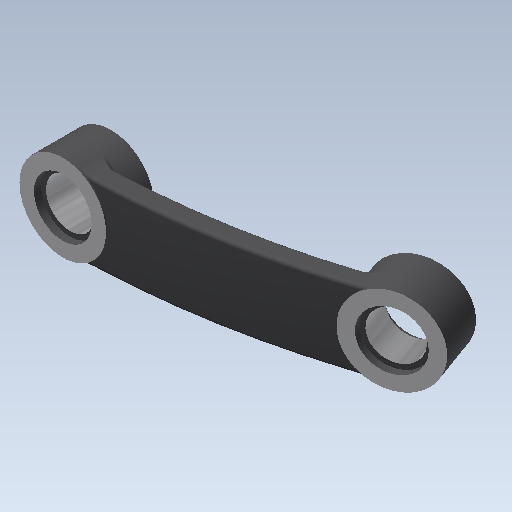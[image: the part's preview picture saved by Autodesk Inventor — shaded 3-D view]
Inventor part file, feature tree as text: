
AUTODESK INVENTOR PART (.ipt)
format: ipt  version: 2020.1 (Build 241239000, 239)  size: 294,912 bytes
history: native  units: mm
features: hole x6, sketch x5, plane x3, extrude x3, fillet x3, other x2, thicken_offset x1, revolve x1
ambient origin geometry x8: Origin, YZ Plane, XZ Plane, XY Plane, X Axis, Y Axis, Z Axis, Center Point
bodies: Solid1 (feature_tree)
feature tree (24):
  sketch  "3D Sketch1"
  plane  "Work Plane1"
  sketch  "Sketch2"  dims[d2=170.0mm d4=170.0mm]
  thicken_offset  "Thicken1"
  extrude  "Extrusion1"  TaperAngle=180.0deg  [1 undecoded]
  plane  "Work Plane2"
  extrude  "Extrusion2"  Depth=170.0mm
  plane  "Work Plane3"
  extrude  "Extrusion3"  Depth=4.0mm
  hole  "Hole1"  [1 undecoded]
  hole  "Hole2"  [1 undecoded]
  fillet  "Fillet1"  Radius=18.0mm
  fillet  "Fillet2"  Radius=10.0mm
  fillet  "Fillet3"  Radius=10.0mm
  hole  "Hole4"  [1 undecoded]
  hole  "Hole5"  [1 undecoded]
  hole  "Hole6"  [1 undecoded]
  hole  "Hole7"  [1 undecoded]
  sketch  "Sketch1"  dims[d0=170.0mm d1=180.0deg]
  other  "Srf1"
  sketch  "Sketch3"  dims[d5=16.0mm d6=4.0mm d7=8.0mm]
  sketch  "Sketch4"  dims[d8=10.0mm d9=0.0mm d10=18.0mm d11=10.0mm d12=0.0mm d13=18.0mm d14=10.0mm d15=0.0mm d16=10.0mm d17=10.0mm d18=10.0mm d19=6.0mm d20=4.0mm d21=2.0mm d22=90.0deg d23=8.0mm d24=20.594885mm d25=10.0mm d26=10.0mm d27=10.0mm d28=6.0mm d29=4.0mm d30=2.0mm d31=90.0deg d32=8.0mm d33=20.594885mm d34=1.0mm d35=10.0mm d36=0.7mm d52=3.490659mm d53=10.0mm d54=10.0mm d55=12.0mm d56=6.0mm d57=4.0mm d58=2.0mm d59=90.0deg d60=1.5mm d61=0.0mm d62=10.0mm d63=10.0mm d64=12.0mm d65=6.0mm d66=4.0mm d67=2.0mm d68=90.0deg d69=1.5mm d70=0.0mm d71=10.0mm d72=10.0mm d73=12.0mm d74=6.0mm d75=4.0mm d76=2.0mm d77=90.0deg d78=1.5mm d79=0.0mm d80=10.0mm d81=10.0mm d82=12.0mm d83=6.0mm d84=4.0mm d85=2.0mm d86=90.0deg d87=1.5mm d88=0.0mm]
  revolve  "RevolutionSrf1"  [1 undecoded]
  other  "3D Intersection1"
note: 8 required parameter values undecoded (feature->parameter linkage not recoverable at this tier; creation-order binding heuristic only, values carry confidence <= 0.55)